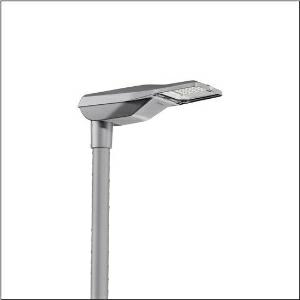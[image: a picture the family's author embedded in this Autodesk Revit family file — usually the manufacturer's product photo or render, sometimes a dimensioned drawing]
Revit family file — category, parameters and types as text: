
# Revit family: streetlight_sl_21_iq_micro___p0_8a_5xe1u31g08db_89ec
name_source: partatom
category: Lighting Fixtures
units: mm (PartAtom-declared; Revit-internal decimal feet)

## family parameters
Cut with Voids When Loaded = No
Host = Face
Light Source = No
Part Type = Normal
Room Calculation Point = No
Round Connector Dimension = Use Diameter
Shared = No

## types (1)
- --- (1 x LED, 4750 lm, 36.4 W, 3000K)
    Apparent Load = 36 VA
    CIE Flux Codes = 33 69 96 100 100
    Color Rendering = 70
    Color Temperature = 3000K
    Default Elevation = 1800 mm
    Description = Streetlight SL 21 iQ micro, mast luminaire, primary light control with lens, of PMMA, primary optical cover: cover, of toughened safety glass, transparent, light distribution: P0.8a, light emission: direct distribution, primary light characteristic: asymmetric, installation type: post-top, side-entry, LED, High Power LED, rated luminous flux: 4.750lm, luminous efficacy: 131lm/W, light colour: 730, colour temperature: 3000K, control gear: iQ Street-Remote, control: pre-setting: linear dimming characteristic, Street-Remote, Auto-Match, Temp-Guard, Lumen-Switch, Night-Set, Smart-Wire, Light-Fading, Desk-Remote (wireless, voltage-free reading and setting of iQ features in the workshop via application-optimized NFC function/RFID function), optimised constant luminous flux control (CLO 2.0), mains connection: 220..240V, AC, 50/60Hz, start of lifetime: 36W, end of service life: 38W, reduction: 16W, luminaire housing, of diecast aluminium, powder-coated, SITECO metallic grey (DB 702S), corrosivity category C5 high according to DIN EN ISO 12944, please order mast flange separately, inclination adjustable: 0°, 5°, 10°, 15°, sealing non-destructively replaceable, multi-level sealing system, length: 528mm, width: 235mm, height: 110mm, mast flange for spigot size: 42mm (side-entry): 5XC10008XM4, 60/48mm (side-entry/post-top): 5XC10108XM2, 76/60mm (side-entry/post-top): 5XC10108XM1, protection rating (complete): IP66, insulation class (complete): insulation class II (safety insulation), certification: CE, ENEC, ENEC+, VDE, impact resistance: IK10, permissible operating ambient temperature for outdoor applications: -40..+50°C, standard-compliant lighting for roads and squares, packaging unit: 1 piece

Light Distribution: P0.8a
    Height = 110 mm
    Lamp = 1 x LED
    Lamp Light Flux = 4750 lm
    Lamp Power = 36.4 W
    Lamp count = 1
    Length = 528 mm
    Luminous efficacy = 130 lm/W
    Manufacturer = Siteco
    ModVariant = No
    Model = 5XE1U31G08DB
    Number of Poles = 1
    OnlyDefault = Yes
    Power Factor = 1
    Product Name = Streetlight SL 21 iQ micro | P0.8a
    Product group = mast luminaire | pylon top
    ProductGroupID = 6100
    Protection Class = Protection class II
    Protection Degree = IP 66
    RLX_Detail_Level = 1
    RLX_Emergency_Light_Flux = 0 lm
    RLX_Emergency_Type = 0
    RLX_Emergency_Type_DB = No
    RlxData = <blob elided: 99557 chars, md5=1bb28d6d>
    Socket = socket
    Standby Power = 0 W
    System Light Flux = 4750 lm
    System Power = 36 W
    Type Comments = factory setting: luminous flux: 100 % | dim-lin: 254 | 715 mA
    Type Image = l_1006881.jpg
    URL = http://relux.com
    VarID = @adj_080817
    Voltage = 0 V
    Weight = 0.00 kg
    Width = 235 mm

## geometry (parser evidence)
native form markers: Blend x4, Sweep x10
no freeform markers — native parametric forms only
